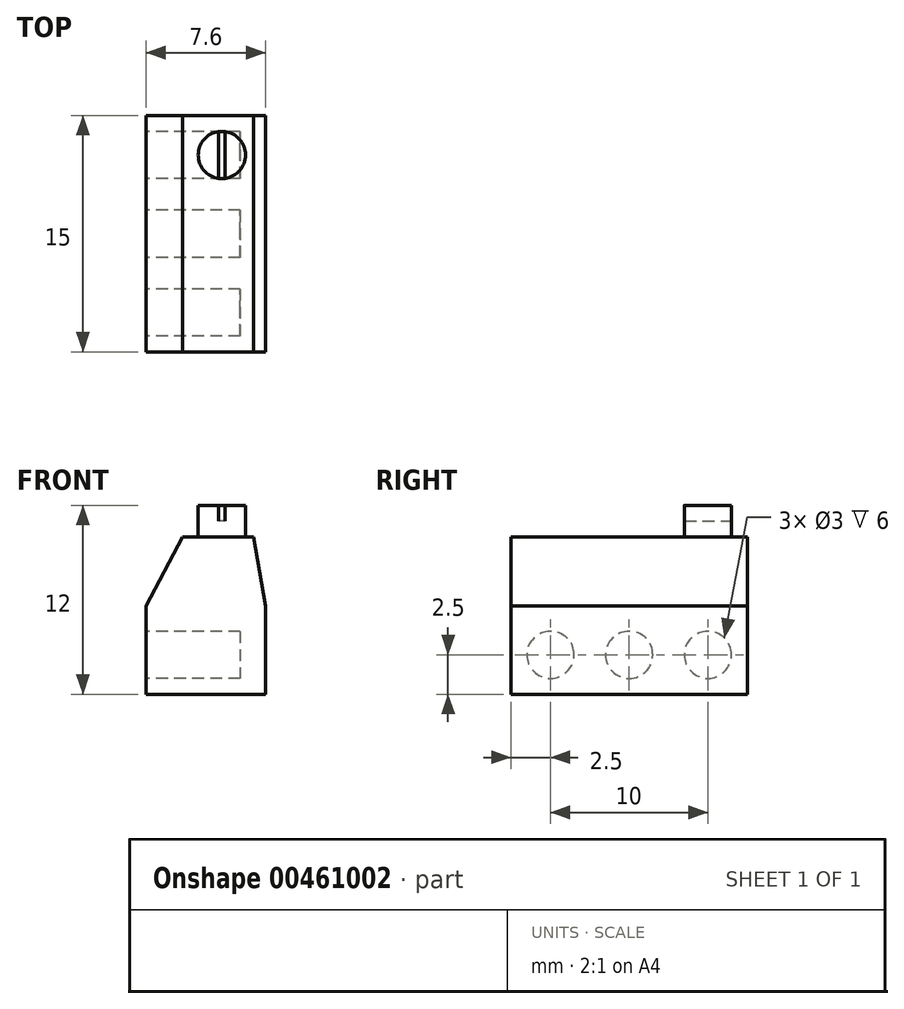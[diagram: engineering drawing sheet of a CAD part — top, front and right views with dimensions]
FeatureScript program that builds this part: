
annotation { "Feature Type Name" : "Feature", "Feature Type Description" : "" }
export const myFeature = defineFeature(function(context is Context, id is Id, definition is map)
    precondition{}
    {
        {
            var Q0;
            Q0=qCreatedBy(makeId("Front.planeOp"),FACE);
            var sketch = newSketch(context, id + "F0", { "sketchPlane" : qUnion([Q0])});
            skLineSegment(sketch, "E0", {"start": v(0, 0) * mm, "end": v(0, 5.62) * mm});
            skLineSegment(sketch, "E1", {"start": v(0, 5.62) * mm, "end": v(2.33, 10) * mm});
            skLineSegment(sketch, "E2", {"start": v(2.33, 10) * mm, "end": v(6.83, 10) * mm});
            skLineSegment(sketch, "E3", {"start": v(6.83, 10) * mm, "end": v(7.6, 5.62) * mm});
            skLineSegment(sketch, "E4", {"start": v(7.6, 5.62) * mm, "end": v(7.6, 0) * mm});
            skLineSegment(sketch, "E5", {"start": v(7.6, 0) * mm, "end": v(0, 0) * mm});
            skSolve(sketch);
        }
        {
            var Q0;
            Q0 = qSketchRegion(id + "F0", true);
            extrude(context, id + "F1", {"entities" : qUnion([Q0]), "depth" : 15 * mm});
        }
        {
            var Q0;
            Q0=makeQuery(id+"F1.opExtrude","SWEPT_FACE",FACE,{"disambiguationData":[OSD([sQuery(id+"F0.wireOp",EDGE,"E0")])]});
            var sketch = newSketch(context, id + "F2", { "sketchPlane" : qUnion([Q0])});
            skCircle(sketch, "E6", {"center": v(2.5, 2.5) * mm, "radius": 1.5 * mm});
            skCircle(sketch, "E7", {"center": v(7.5, 2.5) * mm, "radius": 1.5 * mm});
            skCircle(sketch, "E8", {"center": v(12.5, 2.5) * mm, "radius": 1.5 * mm});
            skSolve(sketch);
        }
        {
            var Q0;
            Q0 = qSketchRegion(id + "F2", true);
            extrude(context, id + "F3", {"entities" : qUnion([Q0]), "operationType" : NewBodyOperationType.REMOVE, "oppositeDirection" : true, "depth" : 6 * mm});
        }
        {
            var Q0;
            Q0=makeQuery(id+"F1.opExtrude","SWEPT_FACE",FACE,{"disambiguationData":[OSD([sQuery(id+"F0.wireOp",EDGE,"E2")])]});
            var sketch = newSketch(context, id + "F4", { "sketchPlane" : qUnion([Q0])});
            skCircle(sketch, "E9", {"center": v(4.83, -2.5) * mm, "radius": 1.5 * mm});
            skSolve(sketch);
        }
        {
            var Q0;
            Q0 = qSketchRegion(id + "F4", true);
            extrude(context, id + "F5", {"entities" : qUnion([Q0]), "depth" : 2 * mm});
        }
        {
            var Q0;
            Q0=makeQuery(id+"F5.opExtrude","CAP_FACE",FACE,{"disambiguationData":[OSD([sQuery(id+"F4.wireOp",EDGE,"E9")])],"isStart":false});
            var sketch = newSketch(context, id + "F6", { "sketchPlane" : qUnion([Q0])});
            skLineSegment(sketch, "E10.bottom", {"start": v(4.63, -3.99) * mm, "end": v(5.03, -3.99) * mm});
            skLineSegment(sketch, "E10.top", {"start": v(4.63, -1.01) * mm, "end": v(5.03, -1.01) * mm});
            skLineSegment(sketch, "E10.left", {"start": v(4.63, -3.99) * mm, "end": v(4.63, -1.01) * mm});
            skLineSegment(sketch, "E10.right", {"start": v(5.03, -3.99) * mm, "end": v(5.03, -1.01) * mm});
            skPoint(sketch, "E10.middle", {"position": v(4.83, -2.5) * mm});
            skSolve(sketch);
        }
        {
            var Q0;
            Q0 = qSketchRegion(id + "F6", true);
            extrude(context, id + "F7", {"entities" : qUnion([Q0]), "operationType" : NewBodyOperationType.REMOVE, "oppositeDirection" : true, "depth" : 1 * mm});
        }
    });
